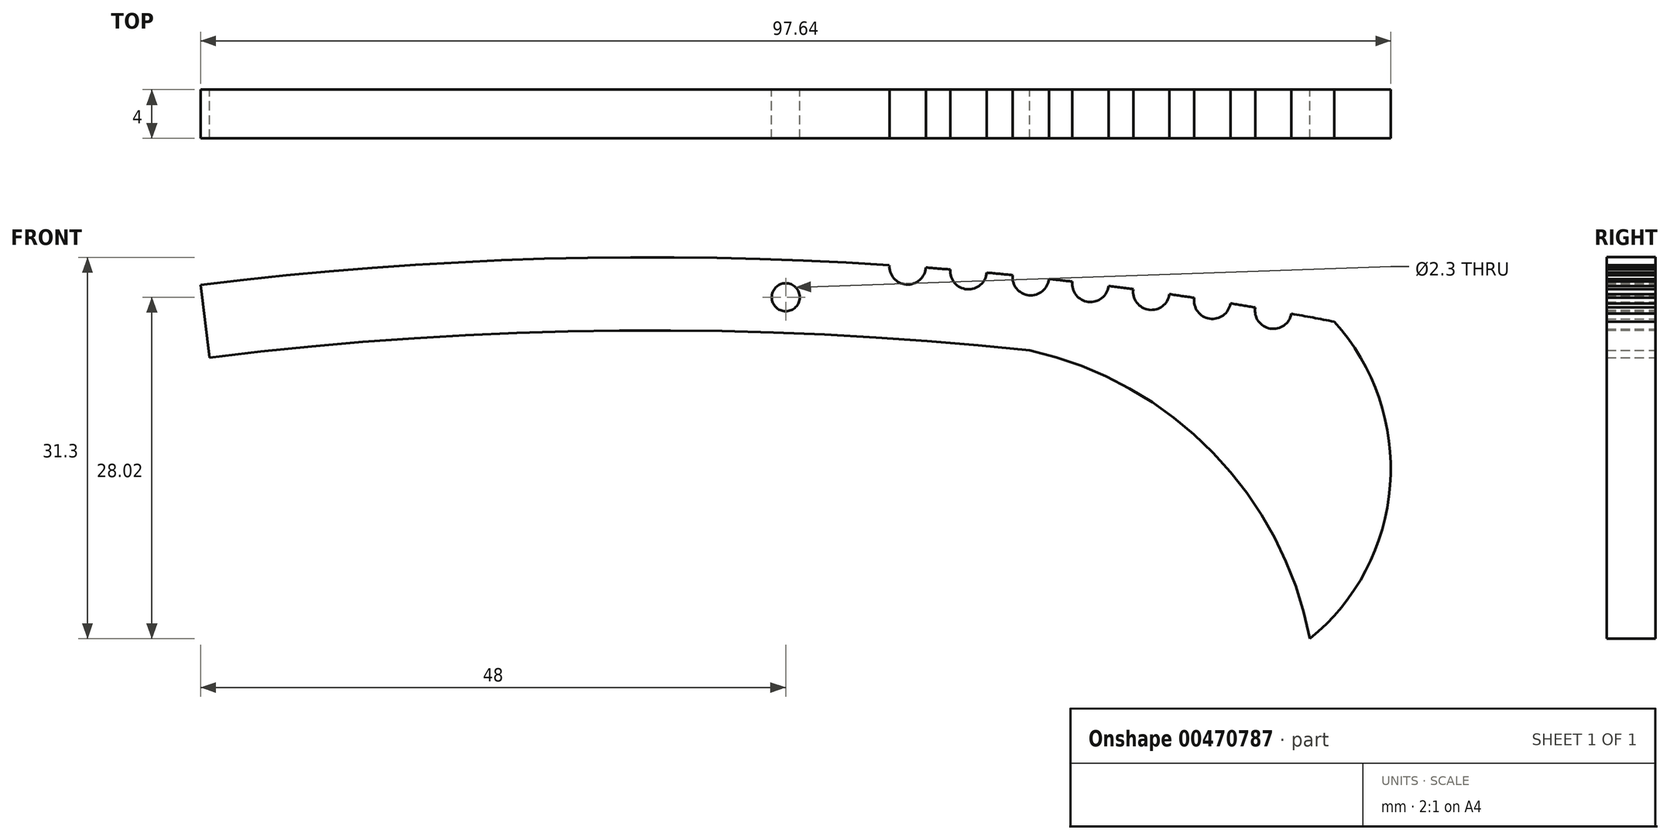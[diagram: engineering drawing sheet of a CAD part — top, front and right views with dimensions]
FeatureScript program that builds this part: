
annotation { "Feature Type Name" : "Feature", "Feature Type Description" : "" }
export const myFeature = defineFeature(function(context is Context, id is Id, definition is map)
    precondition{}
    {
        {
            var Q0;
            Q0=qCreatedBy(makeId("Front.planeOp"),FACE);
            var sketch = newSketch(context, id + "F0", { "sketchPlane" : qUnion([Q0])});
            skArc(sketch, "E0", {"start": v(85, 9) * mm, "mid": v(83.24, 9.33) * mm, "end": v(81.48, 9.65) * mm});
            skArc(sketch, "E1", {"start": v(80, -19) * mm, "mid": v(89.36, -6.22) * mm, "end": v(85, 9) * mm});
            skArc(sketch, "E2.0", {"start": v(60, 6.64) * mm, "mid": v(26.35, 8.27) * mm, "end": v(-7.26, 6.05) * mm});
            skArc(sketch, "E3", {"start": v(83, -17.02) * mm, "mid": v(75.04, -1.74) * mm, "end": v(60, 6.64) * mm});
            skLineSegment(sketch, "E4", {"start": v(-8, 12) * mm, "end": v(-7.26, 6.05) * mm});
            skArc(sketch, "E5", {"start": v(48.5, 13.65) * mm, "mid": v(49.9, 12.05) * mm, "end": v(51.5, 13.43) * mm});
            skArc(sketch, "E6", {"start": v(58.6, 12.81) * mm, "mid": v(59.95, 11.17) * mm, "end": v(61.6, 12.5) * mm});
            skArc(sketch, "E7", {"start": v(53.5, 13.28) * mm, "mid": v(54.87, 11.66) * mm, "end": v(56.5, 13.02) * mm});
            skArc(sketch, "E8", {"start": v(63.51, 12.29) * mm, "mid": v(64.82, 10.62) * mm, "end": v(66.49, 11.93) * mm});
            skArc(sketch, "E9", {"start": v(68.51, 11.66) * mm, "mid": v(69.8, 9.98) * mm, "end": v(71.49, 11.25) * mm});
            skArc(sketch, "E10", {"start": v(73.52, 10.95) * mm, "mid": v(74.77, 9.25) * mm, "end": v(76.48, 10.5) * mm});
            skArc(sketch, "E11", {"start": v(78.52, 10.16) * mm, "mid": v(79.74, 8.43) * mm, "end": v(81.48, 9.65) * mm});
            skArc(sketch, "E12.trimOffspring", {"start": v(48.5, 13.65) * mm, "mid": v(20.21, 14.16) * mm, "end": v(-8, 12) * mm});
            skArc(sketch, "E13.trimOffspring", {"start": v(53.5, 13.28) * mm, "mid": v(52.5, 13.36) * mm, "end": v(51.5, 13.43) * mm});
            skArc(sketch, "E14.trimOffspring", {"start": v(58.6, 12.81) * mm, "mid": v(57.55, 12.92) * mm, "end": v(56.5, 13.02) * mm});
            skArc(sketch, "E15.trimOffspring", {"start": v(63.51, 12.29) * mm, "mid": v(62.55, 12.4) * mm, "end": v(61.6, 12.5) * mm});
            skArc(sketch, "E16.trimOffspring", {"start": v(68.51, 11.66) * mm, "mid": v(67.5, 11.8) * mm, "end": v(66.49, 11.93) * mm});
            skArc(sketch, "E17.trimOffspring", {"start": v(73.52, 10.95) * mm, "mid": v(72.5, 11.1) * mm, "end": v(71.49, 11.25) * mm});
            skArc(sketch, "E18.trimOffspring", {"start": v(78.52, 10.16) * mm, "mid": v(77.5, 10.33) * mm, "end": v(76.48, 10.5) * mm});
            skCircle(sketch, "E19", {"center": v(40, 11) * mm, "radius": 1.15 * mm});
            skSolve(sketch);
        }
        {
            var Q0;
            Q0=qSketchRegion(id+"F0",true);
            extrude(context, id + "F1", {"entities" : qUnion([Q0]), "depth" : 4 * mm});
        }
    });
